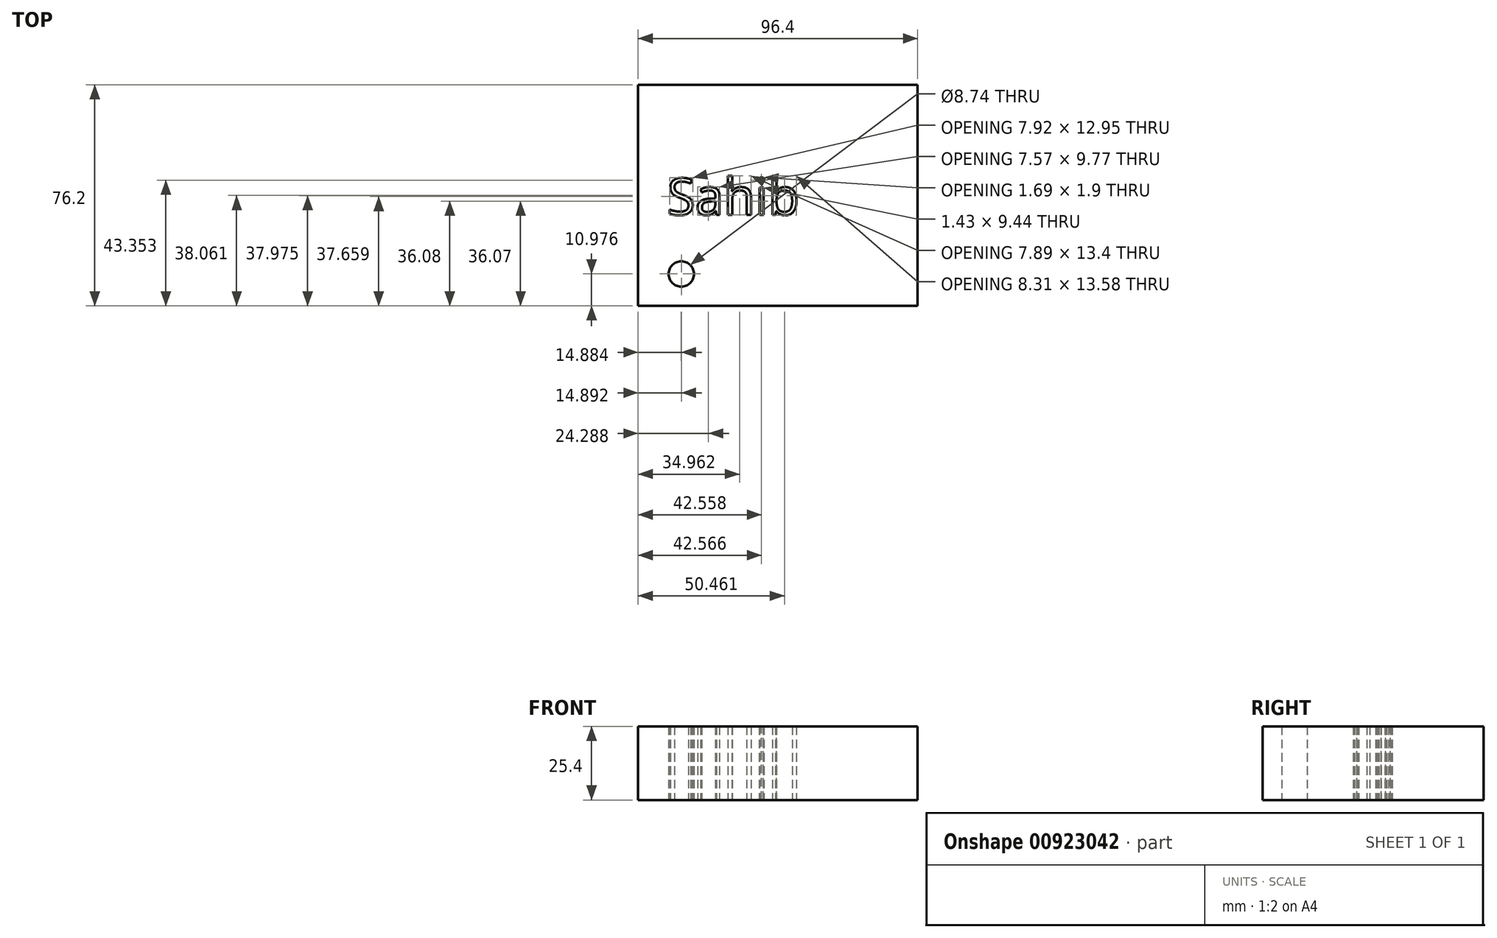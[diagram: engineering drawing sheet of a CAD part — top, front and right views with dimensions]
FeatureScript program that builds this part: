
annotation { "Feature Type Name" : "Feature", "Feature Type Description" : "" }
export const myFeature = defineFeature(function(context is Context, id is Id, definition is map)
    precondition{}
    {
        {
            var Q0;
            Q0=qCreatedBy(makeId("Top.planeOp"),FACE);
            var sketch = newSketch(context, id + "F0", { "sketchPlane" : qUnion([Q0])});
            skText(sketch, "E0", { "text": "Sahib", "fontName": "OpenSans-Regular.ttf"});
            const initialGuessF0  = {"E0": [-0.02622, 0.01478, 1, 0, 0.0127]};
            skSetInitialGuess(sketch, initialGuessF0);
            skSolve(sketch);
        }
        {
            var Q0;
            Q0=qCreatedBy(makeId("Top.planeOp"),FACE);
            var sketch = newSketch(context, id + "F1", { "sketchPlane" : qUnion([Q0])});
            skCircle(sketch, "E1", {"center": v(-21.34, -5.6) * mm, "radius": 4.37 * mm});
            skSolve(sketch);
        }
        {
            var Q0;
            Q0=makeQuery(id+"F1.imprint","IMPRINT",FACE,{"disambiguationData":[TD([[makeQuery(id+"F1.imprint","IMPRINT",EDGE,{"derivedFrom":sQuery(id+"F1.wireOp",EDGE,"E1")}),1.0]])]});
            var sketch = newSketch(context, id + "F2", { "sketchPlane" : qUnion([Q0])});
            skLineSegment(sketch, "E2.bottom", {"start": v(-36.23, -16.58) * mm, "end": v(60.17, -16.58) * mm});
            skLineSegment(sketch, "E2.top", {"start": v(-36.23, 59.62) * mm, "end": v(60.17, 59.62) * mm});
            skLineSegment(sketch, "E2.left", {"start": v(-36.23, -16.58) * mm, "end": v(-36.23, 59.62) * mm});
            skLineSegment(sketch, "E2.right", {"start": v(60.17, -16.58) * mm, "end": v(60.17, 59.62) * mm});
            skSolve(sketch);
        }
        {
            var Q0;
            Q0=makeQuery(id+"F2.imprint","IMPRINT",FACE,{"disambiguationData":[TD([[makeQuery(id+"F2.imprint","IMPRINT",EDGE,{"derivedFrom":sQuery(id+"F2.wireOp",EDGE,"E2.bottom")}),1.0]])]});
            extrude(context, id + "F3", {"entities" : qUnion([Q0]), "depth" : 25.4 * mm, "offsetDistance" : 25.4 * mm});
        }
        {
            var Q0;
            Q0 = qSketchRegion(id + "F0", true);
            extrude(context, id + "F4", {"entities" : qUnion([Q0]), "operationType" : NewBodyOperationType.REMOVE, "depth" : 25.4 * mm, "offsetDistance" : 25.4 * mm});
        }
    });
